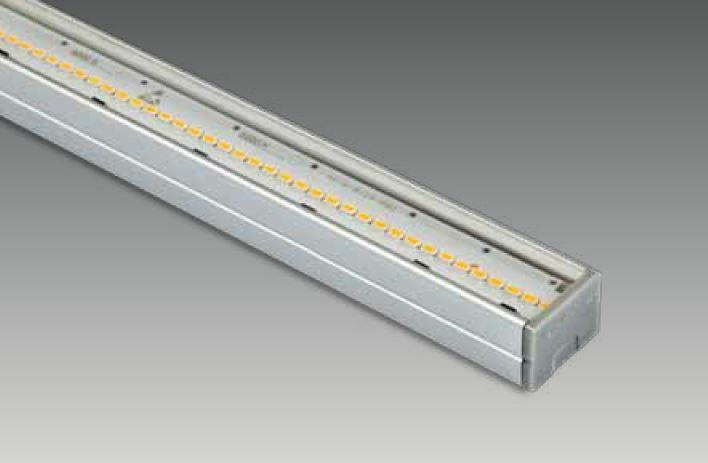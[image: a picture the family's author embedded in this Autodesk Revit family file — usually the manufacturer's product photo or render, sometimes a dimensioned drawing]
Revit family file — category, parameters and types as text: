
# Revit family: SD 0500 LIG-II
name_source: partatom
category: Lighting Fixtures
revit_build: Autodesk Revit 2016 (Build: 20150714_1515(x64)
units: mm (PartAtom-declared; Revit-internal decimal feet)

## family parameters
Cut with Voids When Loaded = No
Host = Face
Light Source = Yes
Part Type = Normal
Room Calculation Point = No
Round Connector Dimension = Use Diameter
Shared = No

## types (1)
- SDLIG.500.10.30.110
    Color Filter = 16777215
    Default Elevation = 1219 mm
    Dimming Lamp Color Temperature Shift = <None>
    Emit Shape Visible in Rendering = Yes
    Emit from Rectangle Length = 20 mm  [stored 0.0656168 ft]
    Emit from Rectangle Width = 500 mm  [stored 1.64042 ft]
    Light Source Symbol Size = 610 mm
    Manufacturer = ARLIGHT
    Type Image = SD 0500 LIG.JPG
    Wattage Comments = 10

note: [stored X ft] marks values corroborated as IEEE doubles in the binary element streams (Revit-internal decimal feet)

## geometry (parser evidence)
native form markers: Sweep x3
no freeform markers — native parametric forms only
